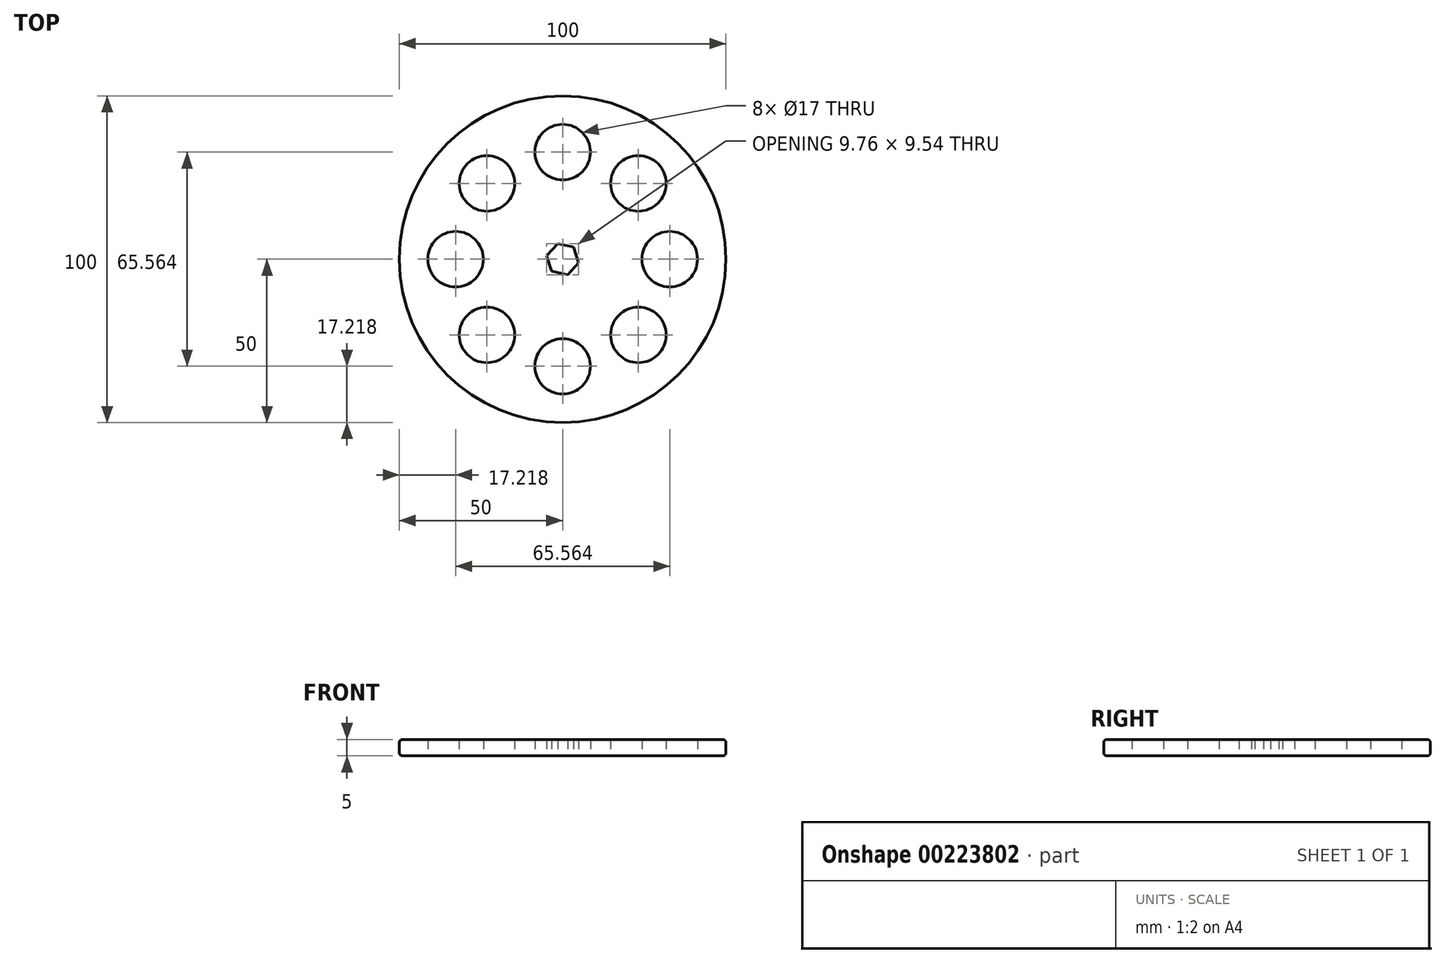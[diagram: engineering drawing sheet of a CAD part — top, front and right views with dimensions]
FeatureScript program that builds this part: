
annotation { "Feature Type Name" : "Feature", "Feature Type Description" : "" }
export const myFeature = defineFeature(function(context is Context, id is Id, definition is map)
    precondition{}
    {
        {
            var Q0;
            Q0=qCreatedBy(makeId("Top.planeOp"),FACE);
            var sketch = newSketch(context, id + "F0", { "sketchPlane" : qUnion([Q0])});
            skCircle(sketch, "E0", {"center": v(0, 0) * mm, "radius": 50 * mm});
            skCircle(sketch, "E1.cCircle", {"center": v(0, 0) * mm, "radius": 4.33 * mm, "construction": true});
            skLineSegment(sketch, "E1.0", {"start": v(4.88, -1.09) * mm, "end": v(1.5, -4.77) * mm});
            skLineSegment(sketch, "E1.1", {"start": v(1.5, -4.77) * mm, "end": v(-3.38, -3.68) * mm});
            skLineSegment(sketch, "E1.2", {"start": v(-3.38, -3.68) * mm, "end": v(-4.88, 1.09) * mm});
            skLineSegment(sketch, "E1.3", {"start": v(-4.88, 1.09) * mm, "end": v(-1.5, 4.77) * mm});
            skLineSegment(sketch, "E1.4", {"start": v(-1.5, 4.77) * mm, "end": v(3.38, 3.68) * mm});
            skLineSegment(sketch, "E1.5", {"start": v(3.38, 3.68) * mm, "end": v(4.88, -1.09) * mm});
            skPoint(sketch, "E1.0.midPoint", {"position": v(3.19, -2.93) * mm});
            skCircle(sketch, "E2", {"center": v(-32.78, 0) * mm, "radius": 8.5 * mm});
            skCircle(sketch, "E3.1.0", {"center": v(-23.18, -23.18) * mm, "radius": 8.5 * mm});
            skCircle(sketch, "E3.2.0", {"center": v(0, -32.78) * mm, "radius": 8.5 * mm});
            skCircle(sketch, "E3.3.0", {"center": v(23.18, -23.18) * mm, "radius": 8.5 * mm});
            skCircle(sketch, "E4.1.4.0", {"center": v(32.78, 0) * mm, "radius": 8.5 * mm});
            skCircle(sketch, "E5.1.5.0", {"center": v(23.18, 23.18) * mm, "radius": 8.5 * mm});
            skCircle(sketch, "E6.1.6.0", {"center": v(0, 32.78) * mm, "radius": 8.5 * mm});
            skCircle(sketch, "E7.1.7.0", {"center": v(-23.18, 23.18) * mm, "radius": 8.5 * mm});
            skSolve(sketch);
        }
        {
            var Q0;
            Q0=makeQuery(id+"F0.imprint","IMPRINT",FACE,{"disambiguationData":[TD([[makeQuery(id+"F0.imprint","IMPRINT",EDGE,{"derivedFrom":sQuery(id+"F0.wireOp",EDGE,"E0")}),1.0]])]});
            extrude(context, id + "F1", {"entities" : qUnion([Q0]), "depth" : 5 * mm});
        }
        {
            var Q0;
            Q0=makeQuery(id+"F1.opExtrude","CAP_EDGE",EDGE,{"disambiguationData":[OSD([sQuery(id+"F0.wireOp",EDGE,"E0")])],"isStart":false});
            var Q1;
            Q1=makeQuery(id+"F1.opExtrude","CAP_EDGE",EDGE,{"disambiguationData":[OSD([sQuery(id+"F0.wireOp",EDGE,"E0")])],"isStart":true});
            fillet(context, id + "F2", {"entities" : qUnion([Q0, Q1]), "radius" : 1 * mm, "tangentPropagation" : true, "allowEdgeOverflow" : false});
        }
    });
